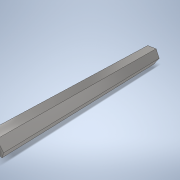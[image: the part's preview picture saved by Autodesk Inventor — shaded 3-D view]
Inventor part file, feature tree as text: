
AUTODESK INVENTOR PART (.ipt)
format: ipt  version: 2020 (Build 240168000, 168)  size: 103,424 bytes
history: native  units: in
note: dims shown in document units (in); Inventor stores cm internally (conversion verified against a paired STEP export)
features: extrude x1, sketch x1
ambient origin geometry x8: Origin, YZ Plane, XZ Plane, XY Plane, X Axis, Y Axis, Z Axis, Center Point
bodies: Solid1 (feature_tree)
feature tree (2):
  extrude  "Extrusion1"  Depth=4.0in TaperAngle=0.0deg
  sketch  "Sketch1"  dims[d0=0.5in d1=4.0in d2=0.0in]
